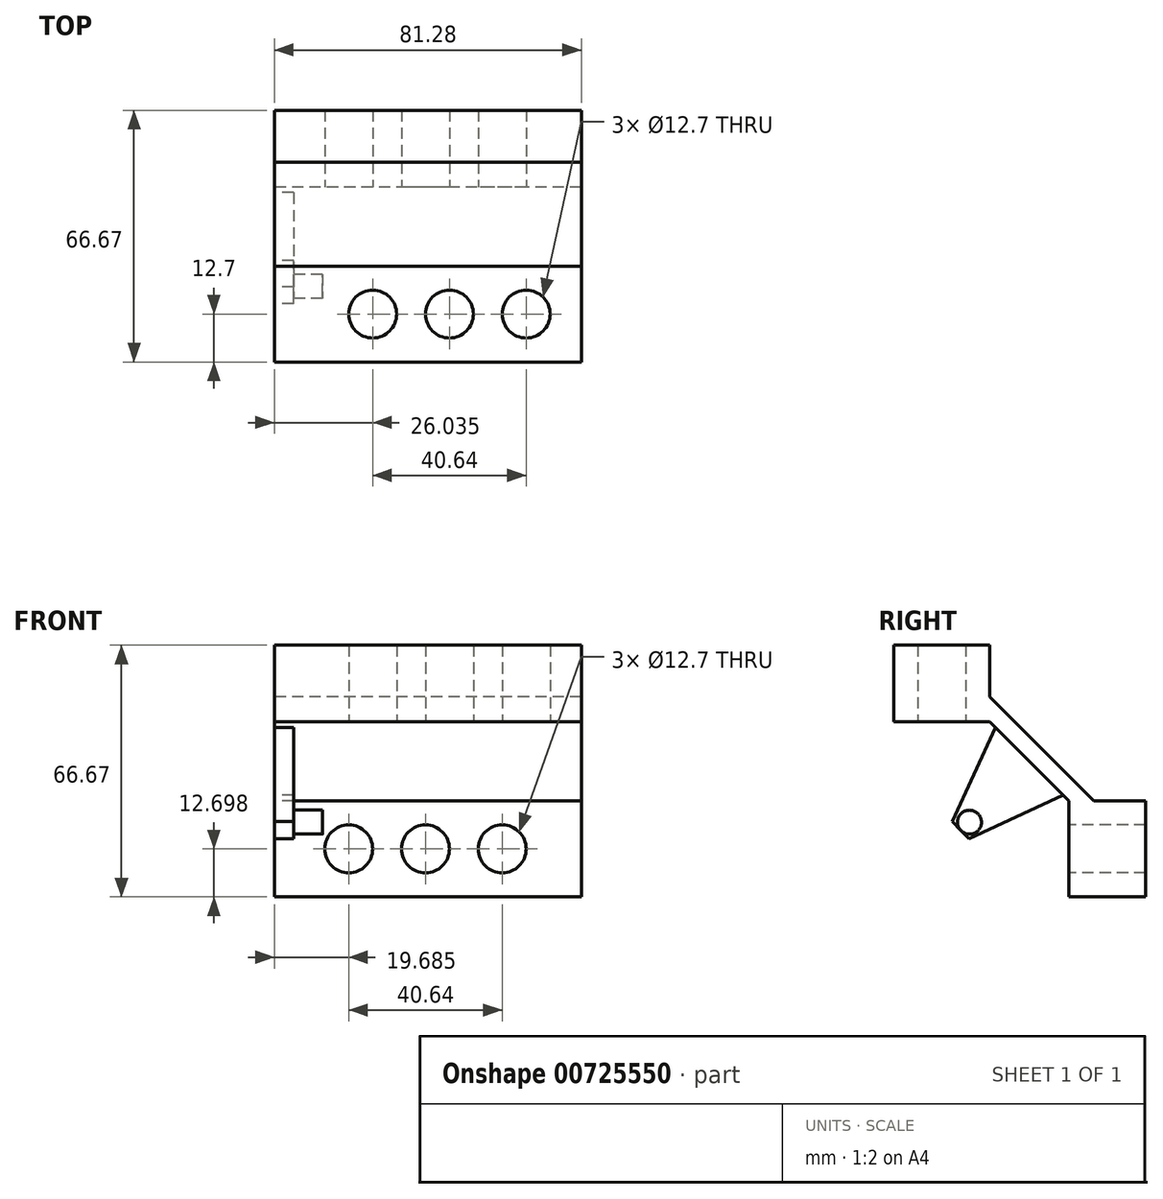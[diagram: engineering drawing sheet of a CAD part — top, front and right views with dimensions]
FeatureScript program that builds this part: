
annotation { "Feature Type Name" : "Feature", "Feature Type Description" : "" }
export const myFeature = defineFeature(function(context is Context, id is Id, definition is map)
    precondition{}
    {
        {
            var Q0;
            Q0=qCreatedBy(makeId("Front.planeOp"),FACE);
            var sketch = newSketch(context, id + "F0", { "sketchPlane" : qUnion([Q0])});
            skLineSegment(sketch, "E0.bottom", {"start": v(-38.1, 0) * mm, "end": v(38.1, 0) * mm});
            skLineSegment(sketch, "E0.top", {"start": v(-38.1, 25.4) * mm, "end": v(38.1, 25.4) * mm});
            skLineSegment(sketch, "E0.left", {"start": v(-38.1, 0) * mm, "end": v(-38.1, 25.4) * mm});
            skLineSegment(sketch, "E0.right", {"start": v(38.1, 0) * mm, "end": v(38.1, 25.4) * mm});
            skPoint(sketch, "E0.middle", {"position": v(0, 12.7) * mm});
            skSolve(sketch);
        }
        {
            var Q0;
            Q0=makeQuery(id+"F0.imprint","IMPRINT",FACE,{"disambiguationData":[TD([[makeQuery(id+"F0.imprint","IMPRINT",EDGE,{"derivedFrom":sQuery(id+"F0.wireOp",EDGE,"E0.bottom")}),1.0]])]});
            extrude(context, id + "F1", {"entities" : qUnion([Q0]), "depth" : 25.4 * mm, "offsetDistance" : 25.4 * mm});
        }
        {
            var Q0;
            Q0=makeQuery(id+"F1.opExtrude","SWEPT_FACE",FACE,{"disambiguationData":[OSD([sQuery(id+"F0.wireOp",EDGE,"E0.bottom")])]});
            var sketch = newSketch(context, id + "F2", { "sketchPlane" : qUnion([Q0])});
            skCircle(sketch, "E1", {"center": v(3.18, 12.7) * mm, "radius": 6.35 * mm});
            skCircle(sketch, "E2", {"center": v(23.5, 12.7) * mm, "radius": 6.35 * mm});
            skCircle(sketch, "E3", {"center": v(-17.15, 12.7) * mm, "radius": 6.35 * mm});
            skSolve(sketch);
        }
        {
            var Q0;
            Q0=makeQuery(id+"F2.imprint","IMPRINT",FACE,{"disambiguationData":[TD([[makeQuery(id+"F2.imprint","IMPRINT",EDGE,{"derivedFrom":sQuery(id+"F2.wireOp",EDGE,"E3")}),1.0]])]});
            var Q1;
            Q1=makeQuery(id+"F2.imprint","IMPRINT",FACE,{"disambiguationData":[TD([[makeQuery(id+"F2.imprint","IMPRINT",EDGE,{"derivedFrom":sQuery(id+"F2.wireOp",EDGE,"E1")}),1.0]])]});
            var Q2;
            Q2=makeQuery(id+"F2.imprint","IMPRINT",FACE,{"disambiguationData":[TD([[makeQuery(id+"F2.imprint","IMPRINT",EDGE,{"derivedFrom":sQuery(id+"F2.wireOp",EDGE,"E2")}),1.0]])]});
            extrude(context, id + "F3", {"entities" : qUnion([Q0, Q1, Q2]), "operationType" : NewBodyOperationType.REMOVE, "oppositeDirection" : true, "depth" : 25.4 * mm, "offsetDistance" : 25.4 * mm});
        }
        {
            var Q0;
            Q0=qCreatedBy(makeId("Right.planeOp"),FACE);
            var sketch = newSketch(context, id + "F4", { "sketchPlane" : qUnion([Q0])});
            skLineSegment(sketch, "E4", {"start": v(0, 25.45) * mm, "end": v(-64.3, -38.85) * mm});
            skLineSegment(sketch, "E5", {"start": v(0, 0) * mm, "end": v(-48.66, -48.66) * mm});
            skLineSegment(sketch, "E6", {"start": v(20.95, 0) * mm, "end": v(-40.19, -61.14) * mm});
            skSolve(sketch);
        }
        {
            var Q0;
            Q0=sQuery(id+"F4.wireOp",EDGE,"E6");
            cPlane(context, id + "F5", {"entities" : qUnion([Q0]), "cplaneType" : CPlaneType.LINE_ANGLE, "offset" : 25.4 * mm, "angle" : 0 * degree, "width" : 152.4 * mm, "height" : 152.4 * mm});
        }
        {
            var Q0;
            Q0=makeQuery(id+"F1.opExtrude","SWEPT_BODY",BODY,{"disambiguationData":[OSD([sQuery(id+"F0.wireOp",EDGE,"E0.bottom"),sQuery(id+"F0.wireOp",EDGE,"E0.top"),sQuery(id+"F0.wireOp",EDGE,"E0.left"),sQuery(id+"F0.wireOp",EDGE,"E0.right")])]});
            var Q1;
            Q1=sQuery(id+"F4.wireOp",EDGE,"E6");
            circularPattern(context, id + "F6", {"entities" : qUnion([Q0]), "axis" : qUnion([Q1]), "angle" : 360 * degree, "instanceCount" : 2, "equalSpace" : true});
        }
        {
            var Q0;
            Q0=qCreatedBy(id+"F5.planeOp",FACE);
            var sketch = newSketch(context, id + "F7", { "sketchPlane" : qUnion([Q0])});
            skLineSegment(sketch, "E7", {"start": v(-38.1, 0) * mm, "end": v(38.1, 0) * mm});
            skLineSegment(sketch, "E8", {"start": v(38.1, 0) * mm, "end": v(38.1, 4.66) * mm});
            skLineSegment(sketch, "E9", {"start": v(38.1, 4.66) * mm, "end": v(-38.1, 4.66) * mm});
            skLineSegment(sketch, "E10", {"start": v(-38.1, 4.66) * mm, "end": v(-38.1, 0) * mm});
            skSolve(sketch);
        }
        {
            var Q0;
            Q0=makeQuery(id+"F7.imprint","IMPRINT",FACE,{"disambiguationData":[TD([[makeQuery(id+"F7.imprint","IMPRINT",EDGE,{"derivedFrom":sQuery(id+"F7.wireOp",EDGE,"E7")}),1.0]])]});
            extrude(context, id + "F8", {"entities" : qUnion([Q0]), "endBound" : BoundingType.SYMMETRIC, "depth" : 44.7 * mm, "offsetDistance" : 25.4 * mm});
        }
        {
            var Q0;
            Q0=makeQuery(id+"F6.opPattern","COPY",BODY,{"derivedFrom":makeQuery(id+"F1.opExtrude","SWEPT_BODY",BODY,{"disambiguationData":[OSD([sQuery(id+"F0.wireOp",EDGE,"E0.bottom"),sQuery(id+"F0.wireOp",EDGE,"E0.top"),sQuery(id+"F0.wireOp",EDGE,"E0.left"),sQuery(id+"F0.wireOp",EDGE,"E0.right")])]}),"instanceName":"1"});
            var Q1;
            Q1=makeQuery(id+"F8.opExtrude","SWEPT_BODY",BODY,{"disambiguationData":[OSD([sQuery(id+"F7.wireOp",EDGE,"E7"),sQuery(id+"F7.wireOp",EDGE,"E8"),sQuery(id+"F7.wireOp",EDGE,"E9"),sQuery(id+"F7.wireOp",EDGE,"E10")])]});
            var Q2;
            Q2=makeQuery(id+"F1.opExtrude","SWEPT_BODY",BODY,{"disambiguationData":[OSD([sQuery(id+"F0.wireOp",EDGE,"E0.bottom"),sQuery(id+"F0.wireOp",EDGE,"E0.top"),sQuery(id+"F0.wireOp",EDGE,"E0.left"),sQuery(id+"F0.wireOp",EDGE,"E0.right")])]});
            booleanBodies(context, id + "F9", {"operationType" : BooleanOperationType.UNION, "tools" : qUnion([Q0, Q1, Q2])});
        }
        {
            var Q0;
            Q0=makeQuery(id+"F9.opBoolean","MERGE",FACE,{"derivedFrom":[makeQuery(id+"F1.opExtrude","SWEPT_FACE",FACE,{"disambiguationData":[OSD([sQuery(id+"F0.wireOp",EDGE,"E0.left")])]}),makeQuery(id+"F6.opPattern","COPY",FACE,{"derivedFrom":makeQuery(id+"F1.opExtrude","SWEPT_FACE",FACE,{"disambiguationData":[OSD([sQuery(id+"F0.wireOp",EDGE,"E0.right")])]}),"instanceName":"1"}),makeQuery(id+"F8.opExtrude","SWEPT_FACE",FACE,{"disambiguationData":[OSD([sQuery(id+"F7.wireOp",EDGE,"E8")])]})]});
            extrude(context, id + "F10", {"entities" : qUnion([Q0]), "operationType" : NewBodyOperationType.ADD, "depth" : 5.08 * mm, "offsetDistance" : 25.4 * mm});
        }
        {
            var Q0;
            Q0=makeQuery(id+"F10.opExtrude","CAP_FACE",FACE,{"disambiguationData":[OSD([sQuery(id+"F0.wireOp",EDGE,"E0.left"),sQuery(id+"F0.wireOp",EDGE,"E0.right"),sQuery(id+"F7.wireOp",EDGE,"E8")])],"isStart":false});
            var sketch = newSketch(context, id + "F11", { "sketchPlane" : qUnion([Q0])});
            skLineSegment(sketch, "E11", {"start": v(0, 0) * mm, "end": v(-20.95, -20.95) * mm});
            skLineSegment(sketch, "E12", {"start": v(9.97, -26.43) * mm, "end": v(5.5, -30.95) * mm});
            skLineSegment(sketch, "E13", {"start": v(9.97, -26.43) * mm, "end": v(-1.5, -1.5) * mm});
            skLineSegment(sketch, "E14", {"start": v(-1.5, -1.5) * mm, "end": v(-19.46, -19.46) * mm});
            skLineSegment(sketch, "E15", {"start": v(-19.46, -19.46) * mm, "end": v(5.5, -30.95) * mm});
            skSolve(sketch);
        }
        {
            var Q0;
            Q0=makeQuery(id+"F11.imprint","IMPRINT",FACE,{"disambiguationData":[TD([[makeQuery(id+"F11.imprint","IMPRINT",EDGE,{"derivedFrom":sQuery(id+"F11.wireOp",EDGE,"E12")}),-1.0]])]});
            extrude(context, id + "F12", {"entities" : qUnion([Q0]), "operationType" : NewBodyOperationType.ADD, "oppositeDirection" : true, "depth" : 5.08 * mm, "offsetDistance" : 25.4 * mm});
        }
        {
            var Q0;
            Q0=makeQuery(id+"F12.opExtrude","CAP_FACE",FACE,{"disambiguationData":[OSD([sQuery(id+"F11.wireOp",EDGE,"E12"),sQuery(id+"F11.wireOp",EDGE,"E13"),sQuery(id+"F11.wireOp",EDGE,"E14"),sQuery(id+"F11.wireOp",EDGE,"E15")])],"isStart":false});
            var sketch = newSketch(context, id + "F13", { "sketchPlane" : qUnion([Q0])});
            skCircle(sketch, "E16", {"center": v(-5.36, -26.58) * mm, "radius": 3.18 * mm});
            skSolve(sketch);
        }
        {
            var Q0;
            Q0=makeQuery(id+"F13.imprint","IMPRINT",FACE,{"disambiguationData":[TD([[makeQuery(id+"F13.imprint","IMPRINT",EDGE,{"derivedFrom":sQuery(id+"F13.wireOp",EDGE,"E16")}),1.0]])]});
            extrude(context, id + "F14", {"entities" : qUnion([Q0]), "operationType" : NewBodyOperationType.ADD, "depth" : 7.67 * mm, "offsetDistance" : 25.4 * mm});
        }
        {
            var Q0;
            {var subQ0=sQuery(id+"F0.wireOp",EDGE,"E0.top");Q0=makeQuery(id+"F10.boolean.opBoolean","MERGE",FACE,{"derivedFrom":[makeQuery(id+"F1.opExtrude","SWEPT_FACE",FACE,{"disambiguationData":[OSD([subQ0])]}),makeQuery(id+"F10.opExtrude","SWEPT_FACE",FACE,{"disambiguationData":[OSD([subQ0,sQuery(id+"F0.wireOp",EDGE,"E0.left")])]})]});}
            var sketch = newSketch(context, id + "F15", { "sketchPlane" : qUnion([Q0])});
            skPoint(sketch, "E17.0", {"position": v(-43.18, -25.4) * mm});
            skPoint(sketch, "E18.0", {"position": v(38.1, 0) * mm});
            skLineSegment(sketch, "E19.bottom", {"start": v(-43.18, -25.4) * mm, "end": v(38.1, -25.4) * mm});
            skLineSegment(sketch, "E19.top", {"start": v(-43.18, 0) * mm, "end": v(38.1, 0) * mm});
            skLineSegment(sketch, "E19.left", {"start": v(-43.18, -25.4) * mm, "end": v(-43.18, 0) * mm});
            skLineSegment(sketch, "E19.right", {"start": v(38.1, -25.4) * mm, "end": v(38.1, 0) * mm});
            skSolve(sketch);
        }
        {
            var Q0;
            Q0=makeQuery(id+"F15.imprint","IMPRINT",FACE,{"disambiguationData":[TD([[makeQuery(id+"F15.imprint","IMPRINT",EDGE,{"derivedFrom":sQuery(id+"F15.wireOp",EDGE,"E19.bottom")}),1.0]])]});
            extrude(context, id + "F16", {"entities" : qUnion([Q0]), "operationType" : NewBodyOperationType.REMOVE, "oppositeDirection" : true, "depth" : 5.08 * mm, "offsetDistance" : 25.4 * mm});
        }
        {
            var Q0;
            {var subQ0=sQuery(id+"F0.wireOp",EDGE,"E0.top");Q0=makeQuery(id+"F10.boolean.opBoolean","MERGE",FACE,{"derivedFrom":[makeQuery(id+"F6.opPattern","COPY",FACE,{"derivedFrom":makeQuery(id+"F1.opExtrude","SWEPT_FACE",FACE,{"disambiguationData":[OSD([subQ0])]}),"instanceName":"1"}),makeQuery(id+"F10.opExtrude","SWEPT_FACE",FACE,{"disambiguationData":[OSD([subQ0,sQuery(id+"F0.wireOp",EDGE,"E0.right")])]})]});}
            var sketch = newSketch(context, id + "F17", { "sketchPlane" : qUnion([Q0])});
            skPoint(sketch, "E20.0", {"position": v(-38.1, -20.95) * mm});
            skPoint(sketch, "E21.0", {"position": v(43.18, -46.35) * mm});
            skLineSegment(sketch, "E22.bottom", {"start": v(-38.1, -20.95) * mm, "end": v(43.18, -20.95) * mm});
            skLineSegment(sketch, "E22.top", {"start": v(-38.1, -46.35) * mm, "end": v(43.18, -46.35) * mm});
            skLineSegment(sketch, "E22.left", {"start": v(-38.1, -20.95) * mm, "end": v(-38.1, -46.35) * mm});
            skLineSegment(sketch, "E22.right", {"start": v(43.18, -20.95) * mm, "end": v(43.18, -46.35) * mm});
            skSolve(sketch);
        }
        {
            var Q0;
            Q0=makeQuery(id+"F17.imprint","IMPRINT",FACE,{"disambiguationData":[TD([[makeQuery(id+"F17.imprint","IMPRINT",EDGE,{"derivedFrom":sQuery(id+"F17.wireOp",EDGE,"E22.bottom")}),-1.0]])]});
            extrude(context, id + "F18", {"entities" : qUnion([Q0]), "operationType" : NewBodyOperationType.REMOVE, "oppositeDirection" : true, "depth" : 5.08 * mm, "offsetDistance" : 25.4 * mm});
        }
    });
